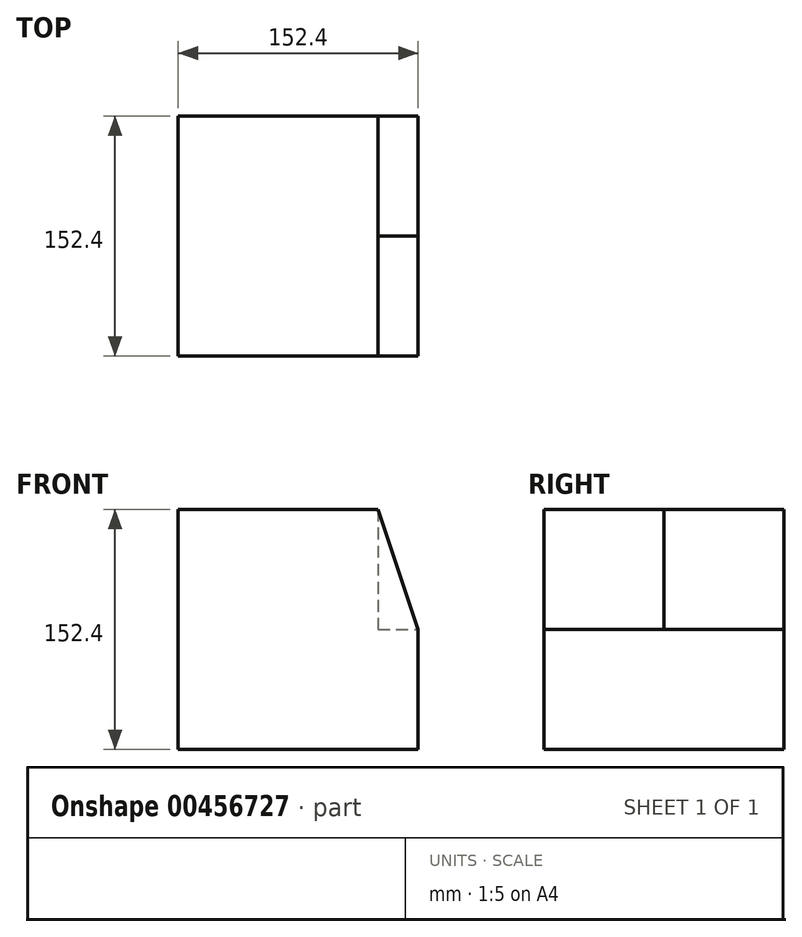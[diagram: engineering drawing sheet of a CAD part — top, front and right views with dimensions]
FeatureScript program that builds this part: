
annotation { "Feature Type Name" : "Feature", "Feature Type Description" : "" }
export const myFeature = defineFeature(function(context is Context, id is Id, definition is map)
    precondition{}
    {
        {
            var Q0;
            Q0=qCreatedBy(makeId("Front.planeOp"),FACE);
            var sketch = newSketch(context, id + "F0", { "sketchPlane" : qUnion([Q0])});
            skLineSegment(sketch, "E0", {"start": v(0, 0) * mm, "end": v(-152.4, 0) * mm});
            skLineSegment(sketch, "E1", {"start": v(-152.4, 0) * mm, "end": v(-152.4, 152.4) * mm});
            skLineSegment(sketch, "E2", {"start": v(-152.4, 152.4) * mm, "end": v(-25.4, 152.4) * mm});
            skLineSegment(sketch, "E3", {"start": v(0, 0) * mm, "end": v(0, 76.2) * mm});
            skLineSegment(sketch, "E4", {"start": v(0, 76.2) * mm, "end": v(-25.4, 152.4) * mm});
            skSolve(sketch);
        }
        {
            var Q0;
            Q0=makeQuery(id+"F0.imprint","IMPRINT",FACE,{"disambiguationData":[TD([[makeQuery(id+"F0.imprint","IMPRINT",EDGE,{"derivedFrom":sQuery(id+"F0.wireOp",EDGE,"E0")}),-1.0]])]});
            extrude(context, id + "F1", {"entities" : qUnion([Q0]), "endBound" : BoundingType.SYMMETRIC, "depth" : 152.4 * mm});
        }
        {
            var Q0;
            Q0=makeQuery(id+"F1.opExtrude","CAP_FACE",FACE,{"disambiguationData":[OSD([sQuery(id+"F0.wireOp",EDGE,"E0"),sQuery(id+"F0.wireOp",EDGE,"E1"),sQuery(id+"F0.wireOp",EDGE,"E2"),sQuery(id+"F0.wireOp",EDGE,"E3"),sQuery(id+"F0.wireOp",EDGE,"E4")])],"isStart":true});
            var sketch = newSketch(context, id + "F2", { "sketchPlane" : qUnion([Q0])});
            skLineSegment(sketch, "E5", {"start": v(0, 76.2) * mm, "end": v(25.4, 152.4) * mm});
            skLineSegment(sketch, "E6", {"start": v(25.4, 152.4) * mm, "end": v(25.4, 76.2) * mm});
            skLineSegment(sketch, "E7", {"start": v(25.4, 76.2) * mm, "end": v(0, 76.2) * mm});
            skSolve(sketch);
        }
        {
            var Q0;
            Q0=makeQuery(id+"F2.imprint","IMPRINT",FACE,{"disambiguationData":[TD([[makeQuery(id+"F2.imprint","IMPRINT",EDGE,{"derivedFrom":sQuery(id+"F2.wireOp",EDGE,"E5")}),-1.0]])]});
            extrude(context, id + "F3", {"entities" : qUnion([Q0]), "operationType" : NewBodyOperationType.REMOVE, "oppositeDirection" : true, "depth" : 76.2 * mm});
        }
    });
